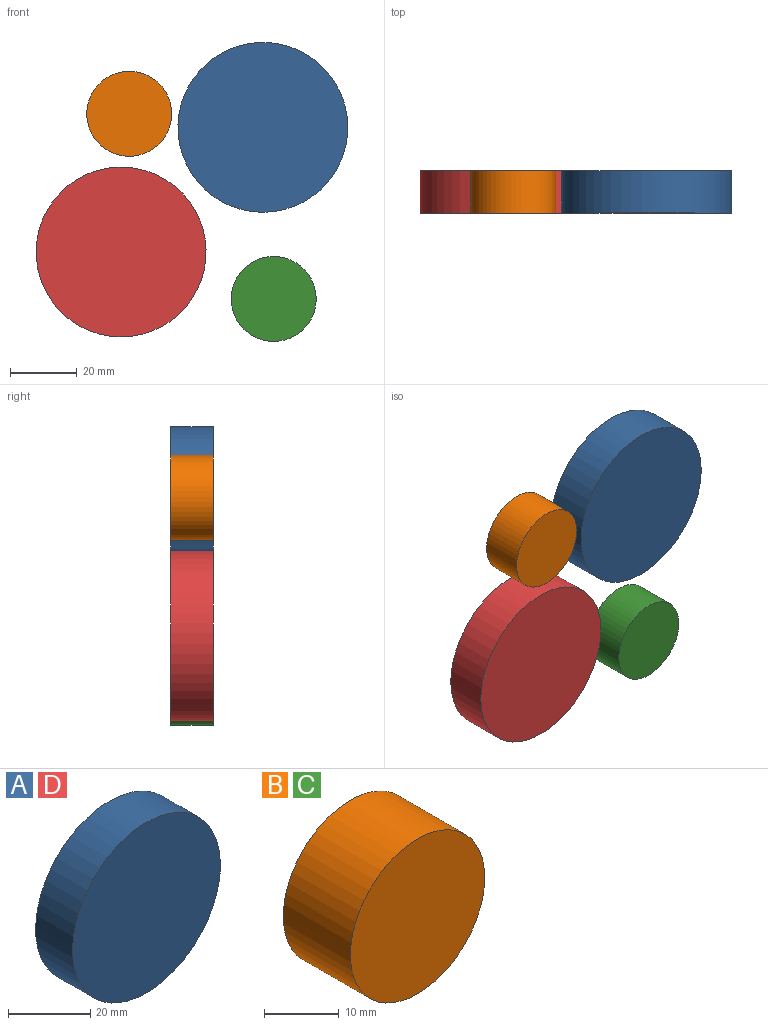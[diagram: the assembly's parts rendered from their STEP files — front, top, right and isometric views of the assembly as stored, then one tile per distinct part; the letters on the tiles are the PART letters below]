
ASSEMBLY  parts=4 mates=3
PART A: 3 faces, bbox 50.8x12.7x50.8 mm
  f0: cylinder r=25.4mm len=50.8mm, axis (0,1,0), area 2026.8mm2, adj f1,f2
  f1: plane 50.8x50.8mm, normal (0,-1,0), area 2026.8mm2, adj f0
  f2: plane 50.8x50.8mm, normal (0,1,0), area 2026.8mm2, adj f0
PART B: 3 faces, bbox 25.4x12.7x25.4 mm
  f0: cylinder r=12.7mm len=25.4mm, axis (0,1,0), area 1013.4mm2, adj f1,f2
  f1: plane 25.4x25.4mm, normal (0,-1,0), area 506.7mm2, adj f0
  f2: plane 25.4x25.4mm, normal (0,1,0), area 506.7mm2, adj f0
PART C: same geometry as B
PART D: same geometry as A
PLACE A t=(37.01,32.26,-6.46)mm
PLACE B t=(-2.95,32.26,-2.41)mm
PLACE C t=(40.24,32.26,-57.78)mm
PLACE D t=(-5.39,32.26,-43.73)mm
MATE planar D.f0 <-> B.f0  axis (0,1,0) through (-5.39,32.26,-43.73)mm
MATE planar D.f0 <-> C.f0  axis (0,1,0) through (-5.39,32.26,-43.73)mm
MATE planar A.f0 <-> D.f0  axis (0,1,0) through (37.01,32.26,-6.46)mm
